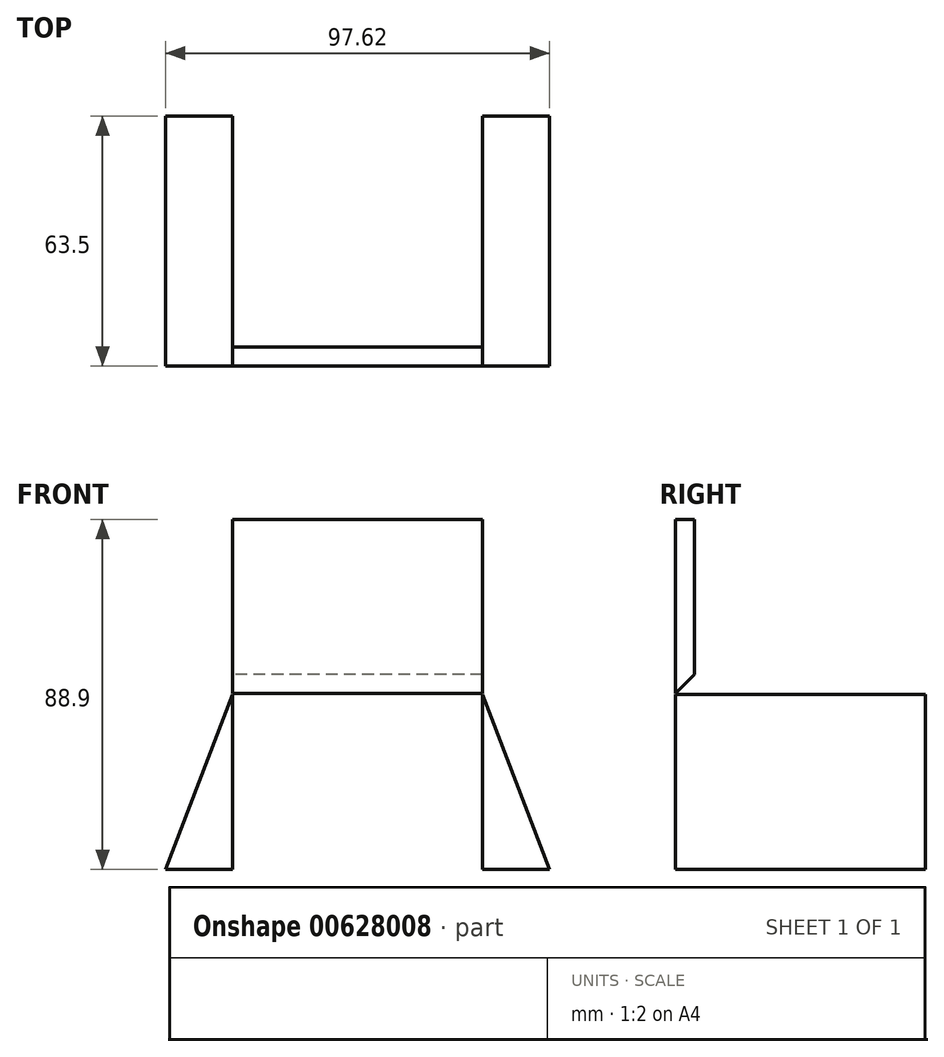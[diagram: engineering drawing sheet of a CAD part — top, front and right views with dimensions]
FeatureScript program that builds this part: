
annotation { "Feature Type Name" : "Feature", "Feature Type Description" : "" }
export const myFeature = defineFeature(function(context is Context, id is Id, definition is map)
    precondition{}
    {
        {
            var Q0;
            Q0=qCreatedBy(makeId("Front.planeOp"),FACE);
            var sketch = newSketch(context, id + "F0", { "sketchPlane" : qUnion([Q0])});
            skLineSegment(sketch, "E0.bottom", {"start": v(-31.75, -44.45) * mm, "end": v(31.75, -44.45) * mm});
            skLineSegment(sketch, "E0.top", {"start": v(-31.75, 44.45) * mm, "end": v(31.75, 44.45) * mm});
            skLineSegment(sketch, "E0.left", {"start": v(-31.75, -44.45) * mm, "end": v(-31.75, 44.45) * mm});
            skLineSegment(sketch, "E0.right", {"start": v(31.75, -44.45) * mm, "end": v(31.75, 44.45) * mm});
            skPoint(sketch, "E0.middle", {"position": v(0, 0) * mm});
            skLineSegment(sketch, "E1.bottom", {"start": v(-48.8, -44.45) * mm, "end": v(48.8, -44.45) * mm});
            skLineSegment(sketch, "E1.top", {"start": v(-48.8, 44.45) * mm, "end": v(48.8, 44.45) * mm});
            skLineSegment(sketch, "E1.left", {"start": v(-48.8, -44.45) * mm, "end": v(-48.8, 44.45) * mm});
            skLineSegment(sketch, "E1.right", {"start": v(48.8, -44.45) * mm, "end": v(48.8, 44.45) * mm});
            skLineSegment(sketch, "E2.bottom", {"start": v(-31.75, 0) * mm, "end": v(31.75, 0) * mm});
            skLineSegment(sketch, "E2.top", {"start": v(-31.75, 88.9) * mm, "end": v(31.75, 88.9) * mm});
            skLineSegment(sketch, "E2.left", {"start": v(-31.75, 0) * mm, "end": v(-31.75, 88.9) * mm});
            skLineSegment(sketch, "E2.right", {"start": v(31.75, 0) * mm, "end": v(31.75, 88.9) * mm});
            skPoint(sketch, "E2.middle", {"position": v(0, 44.45) * mm});
            skLineSegment(sketch, "E3", {"start": v(-31.75, 0) * mm, "end": v(-48.8, -44.45) * mm});
            skLineSegment(sketch, "E4", {"start": v(-31.75, -44.45) * mm, "end": v(-48.8, -44.45) * mm});
            skLineSegment(sketch, "E5", {"start": v(-31.75, -44.45) * mm, "end": v(-31.75, 0) * mm});
            skLineSegment(sketch, "E6", {"start": v(31.75, 0) * mm, "end": v(48.8, -44.45) * mm});
            skLineSegment(sketch, "E7", {"start": v(48.8, -44.45) * mm, "end": v(31.75, -44.45) * mm});
            skLineSegment(sketch, "E8", {"start": v(31.75, -44.45) * mm, "end": v(31.75, 0) * mm});
            skLineSegment(sketch, "E9", {"start": v(-81.55, 49.89) * mm, "end": v(-77.85, 41.86) * mm});
            skSolve(sketch);
        }
        {
            var Q0;
            Q0=makeQuery(id+"F0.imprint","IMPRINT",FACE,{"disambiguationData":[TD([[makeQuery(id+"F0.imprint","IMPRINT",EDGE,{"derivedFrom":sQuery(id+"F0.wireOp",EDGE,"E3")}),1.0]])]});
            var Q1;
            Q1=makeQuery(id+"F0.imprint","IMPRINT",FACE,{"disambiguationData":[TD([[makeQuery(id+"F0.imprint","IMPRINT",EDGE,{"derivedFrom":sQuery(id+"F0.wireOp",EDGE,"E1.bottom")}),1.0]])]});
            var Q2;
            Q2=makeQuery(id+"F0.imprint","IMPRINT",FACE,{"disambiguationData":[TD([[makeQuery(id+"F0.imprint","IMPRINT",EDGE,{"derivedFrom":sQuery(id+"F0.wireOp",EDGE,"E6")}),-1.0]])]});
            extrude(context, id + "F1", {"entities" : qUnion([Q0, Q1, Q2]), "depth" : 63.5 * mm, "offsetDistance" : 25.4 * mm});
        }
        {
            var Q0;
            {var subQ5=sQuery(id+"F0.wireOp",EDGE,"E2.bottom");Q0=makeQuery(id+"F0.imprint","IMPRINT",FACE,{"disambiguationData":[TD([[makeQuery(id+"F0.imprint","IMPRINT",EDGE,{"derivedFrom":subQ5}),1.0]])]});}
            extrude(context, id + "F2", {"entities" : qUnion([Q0]), "operationType" : NewBodyOperationType.ADD, "depth" : 63.5 * mm, "offsetDistance" : 25.4 * mm, "hasSecondDirection" : true, "secondDirectionOppositeDirection" : false, "secondDirectionDepth" : 58.67 * mm});
        }
        {
            var Q0;
            Q0=makeQuery(id+"F2.opExtrude","CAP_EDGE",EDGE,{"disambiguationData":[OSD([sQuery(id+"F0.wireOp",EDGE,"E2.bottom")])],"isStart":true});
            chamfer(context, id + "F3", {"entities" : qUnion([Q0]), "width" : 5.08 * mm, "tangentPropagation" : true});
        }
    });
